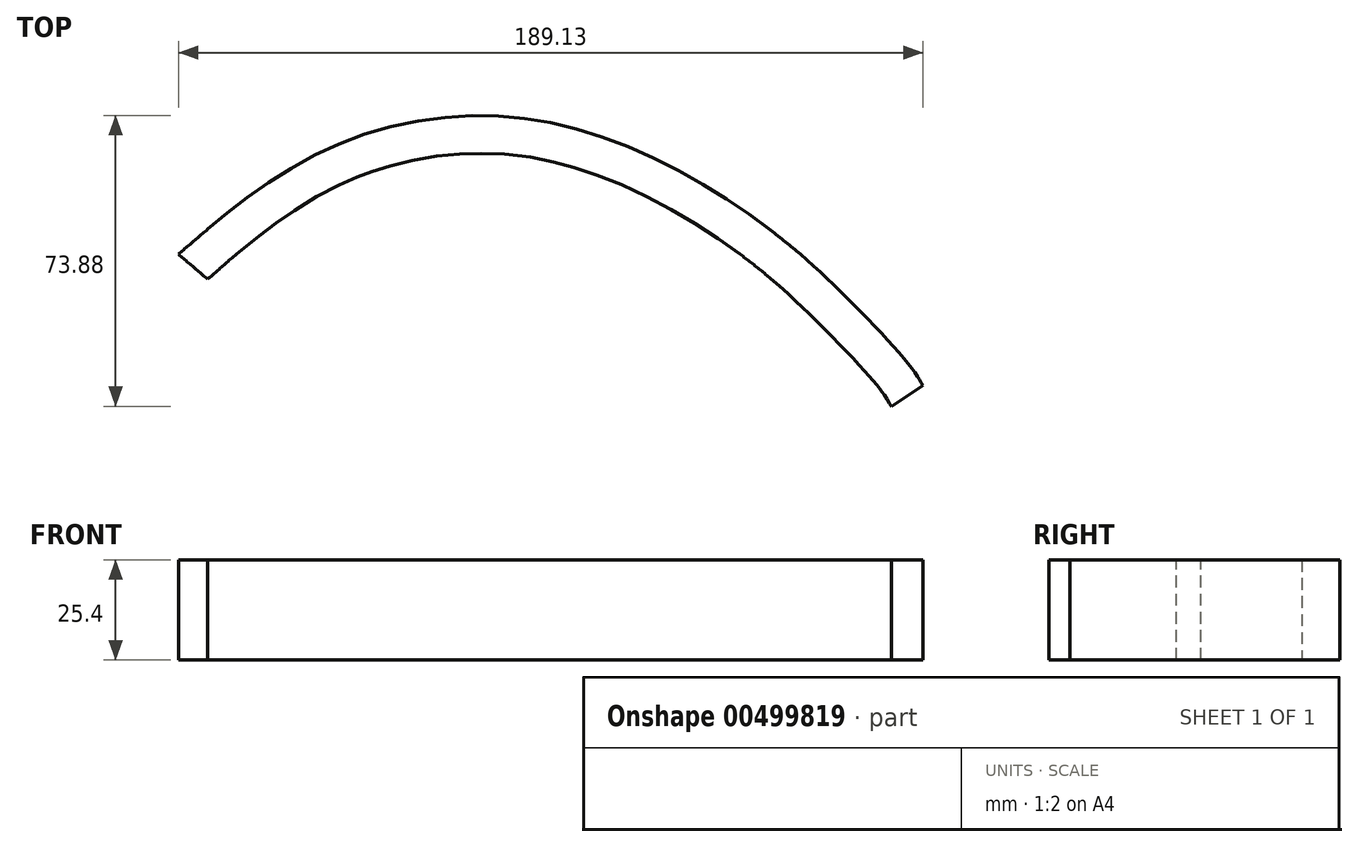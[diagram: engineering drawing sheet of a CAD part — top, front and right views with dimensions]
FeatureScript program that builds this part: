
annotation { "Feature Type Name" : "Feature", "Feature Type Description" : "" }
export const myFeature = defineFeature(function(context is Context, id is Id, definition is map)
    precondition{}
    {
        {
            var Q0;
            Q0=qCreatedBy(makeId("Top.planeOp"),FACE);
            var sketch = newSketch(context, id + "F0", { "sketchPlane" : qUnion([Q0])});
            skFitSpline(sketch, "E0", {"points": [v(0, -39.57) * mm, v(19.12, -23.96) * mm, v(43.28, -10.51) * mm, v(71.59, -4.5) * mm, v(98.2, -6.96) * mm, v(125.64, -17.57) * mm, v(150.11, -33.18) * mm, v(169.77, -50.6) * mm, v(186.21, -68.48) * mm, v(189.13, -72.9) * mm], "startDerivative": vector(163.97, 141.12) * mm, "endDerivative": vector(45.02, -66.87) * mm});
            skLineSegment(sketch, "E1", {"start": v(0, -39.57) * mm, "end": v(190.5, -39.57) * mm, "construction": true});
            skLineSegment(sketch, "E2", {"start": v(181.1, -78.25) * mm, "end": v(189.13, -72.9) * mm});
            skFitSpline(sketch, "E3.0", {"points": [v(3.15, -43.22) * mm, v(6.57, -40.27) * mm, v(11.62, -35.9) * mm, v(17.7, -31.03) * mm, v(21.3, -28.34) * mm, v(24.98, -25.7) * mm, v(29.77, -22.56) * mm, v(35.8, -19.12) * mm, v(41.03, -16.6) * mm, v(45.35, -14.86) * mm, v(49.76, -13.3) * mm, v(55.44, -11.68) * mm, v(62.4, -10.28) * mm, v(68.2, -9.56) * mm, v(72.8, -9.26) * mm, v(77.33, -9.13) * mm, v(82.92, -9.31) * mm, v(89.55, -10.06) * mm, v(95.08, -11.14) * mm, v(99.53, -12.27) * mm, v(104, -13.58) * mm, v(109.61, -15.54) * mm, v(118.55, -19.27) * mm, v(127.3, -23.8) * mm, v(135.62, -28.86) * mm, v(141.59, -32.86) * mm, v(147.23, -37) * mm, v(152.48, -41.19) * mm, v(156.68, -44.83) * mm, v(160.03, -47.9) * mm, v(162.56, -50.3) * mm, v(164.7, -52.37) * mm, v(166.44, -54.1) * mm, v(168.2, -55.85) * mm, v(170.43, -58.1) * mm, v(173.05, -60.82) * mm, v(175.55, -63.48) * mm, v(177.85, -66) * mm, v(179.55, -67.93) * mm, v(180.73, -69.33) * mm, v(181.52, -70.3) * mm, v(182.2, -71.16) * mm, v(182.75, -71.9) * mm, v(183.2, -72.57) * mm, v(183.74, -73.38) * mm, v(184.31, -74.32) * mm, v(184.83, -75.14) * mm, v(185.13, -75.6) * mm], "construction": true});
            skFitSpline(sketch, "E4.MirrorCS", {"points": [v(0, -39.57) * mm, v(19.12, -55.17) * mm, v(43.28, -68.62) * mm, v(71.59, -74.62) * mm, v(98.2, -72.17) * mm, v(125.64, -61.56) * mm, v(150.11, -45.95) * mm, v(169.77, -28.54) * mm, v(186.21, -10.65) * mm, v(189.13, -6.23) * mm], "startDerivative": vector(163.97, -141.12) * mm, "endDerivative": vector(45.02, 66.87) * mm});
            skFitSpline(sketch, "E5.trimOffspring", {"points": [v(6.3, -32.25) * mm, v(9.73, -35.2) * mm, v(14.74, -39.55) * mm, v(20.67, -44.3) * mm, v(24.15, -46.9) * mm, v(27.7, -49.44) * mm, v(32.3, -52.46) * mm, v(38.04, -55.74) * mm, v(42.5, -57.88) * mm, v(45.54, -59.14) * mm, v(47.57, -59.94) * mm, v(50.17, -60.86) * mm, v(53.36, -61.84) * mm, v(57.68, -62.98) * mm, v(63.17, -64.09) * mm, v(68.68, -64.77) * mm, v(73.03, -65.05) * mm, v(77.3, -65.17) * mm, v(82.57, -65) * mm, v(88.82, -64.3) * mm, v(94.03, -63.28) * mm, v(98.25, -62.2) * mm, v(102.5, -60.96) * mm, v(107.88, -59.08) * mm, v(114.33, -56.39) * mm, v(120.7, -53.3) * mm, v(126.96, -49.89) * mm, v(133.02, -46.2) * mm, v(138.82, -42.32) * mm, v(144.3, -38.3) * mm, v(149.39, -34.24) * mm, v(153.47, -30.7) * mm, v(156.74, -27.7) * mm, v(159.22, -25.36) * mm, v(161.32, -23.31) * mm, v(163.04, -21.61) * mm, v(164.78, -19.88) * mm, v(166.98, -17.65) * mm, v(169.56, -14.98) * mm, v(172.01, -12.37) * mm, v(173.89, -10.31) * mm, v(175.25, -8.78) * mm, v(176.18, -7.7) * mm, v(177.03, -6.7) * mm, v(177.76, -5.81) * mm, v(178.26, -5.17) * mm, v(178.6, -4.73) * mm, v(178.89, -4.32) * mm, v(179.2, -3.86) * mm, v(179.65, -3.19) * mm, v(180.07, -2.5) * mm, v(180.61, -1.63) * mm, v(180.94, -1.12) * mm, v(181.12, -0.84) * mm]});
            skFitSpline(sketch, "E6.trimOffspring", {"points": [v(6.3, -46.88) * mm, v(9.73, -43.92) * mm, v(14.74, -39.58) * mm, v(20.67, -34.84) * mm, v(24.15, -32.23) * mm, v(27.7, -29.7) * mm, v(32.3, -26.67) * mm, v(38.04, -23.4) * mm, v(42.5, -21.26) * mm, v(45.54, -20) * mm, v(47.57, -19.2) * mm, v(50.17, -18.27) * mm, v(53.36, -17.3) * mm, v(57.68, -16.15) * mm, v(63.17, -15.04) * mm, v(68.68, -14.37) * mm, v(73.03, -14.08) * mm, v(77.3, -13.96) * mm, v(82.57, -14.13) * mm, v(88.82, -14.84) * mm, v(94.03, -15.85) * mm, v(98.25, -16.93) * mm, v(102.5, -18.17) * mm, v(107.88, -20.05) * mm, v(114.33, -22.74) * mm, v(120.7, -25.82) * mm, v(126.96, -29.24) * mm, v(133.02, -32.93) * mm, v(138.82, -36.81) * mm, v(144.3, -40.83) * mm, v(149.39, -44.9) * mm, v(153.47, -48.44) * mm, v(156.74, -51.43) * mm, v(159.22, -53.77) * mm, v(161.32, -55.82) * mm, v(163.04, -57.52) * mm, v(164.78, -59.25) * mm, v(166.98, -61.48) * mm, v(169.56, -64.15) * mm, v(172.01, -66.76) * mm, v(173.89, -68.82) * mm, v(175.25, -70.35) * mm, v(176.18, -71.43) * mm, v(177.03, -72.42) * mm, v(177.76, -73.32) * mm, v(178.26, -73.96) * mm, v(178.6, -74.4) * mm, v(178.89, -74.8) * mm, v(179.2, -75.27) * mm, v(179.65, -75.95) * mm, v(180.07, -76.63) * mm, v(180.61, -77.5) * mm, v(180.94, -78.01) * mm, v(181.12, -78.29) * mm]});
            skFitSpline(sketch, "E7.trimOffspring", {"points": [v(6.28, -32.27) * mm, v(9.72, -35.22) * mm, v(14.72, -39.56) * mm, v(20.66, -44.31) * mm, v(24.14, -46.92) * mm, v(27.69, -49.46) * mm, v(32.29, -52.48) * mm, v(38.03, -55.76) * mm, v(42.5, -57.9) * mm, v(45.53, -59.16) * mm, v(47.57, -59.96) * mm, v(50.16, -60.88) * mm, v(53.35, -61.86) * mm, v(57.67, -63) * mm, v(63.17, -64.1) * mm, v(68.68, -64.79) * mm, v(73.02, -65.07) * mm, v(77.3, -65.2) * mm, v(82.57, -65.02) * mm, v(88.82, -64.31) * mm, v(94.03, -63.3) * mm, v(98.25, -62.23) * mm, v(102.51, -60.98) * mm, v(107.88, -59.1) * mm, v(114.33, -56.4) * mm, v(120.72, -53.33) * mm, v(126.97, -49.9) * mm, v(133.03, -46.22) * mm, v(138.83, -42.34) * mm, v(144.31, -38.32) * mm, v(149.4, -34.25) * mm, v(153.49, -30.7) * mm, v(156.76, -27.71) * mm, v(159.24, -25.37) * mm, v(161.34, -23.33) * mm, v(163.06, -21.63) * mm, v(164.8, -19.9) * mm, v(167, -17.67) * mm, v(169.57, -15) * mm, v(172.03, -12.38) * mm, v(173.9, -10.33) * mm, v(175.26, -8.8) * mm, v(176.2, -7.72) * mm, v(177.04, -6.72) * mm, v(177.78, -5.83) * mm, v(178.28, -5.18) * mm, v(178.61, -4.74) * mm, v(178.9, -4.34) * mm, v(179.23, -3.88) * mm, v(179.67, -3.2) * mm, v(180.1, -2.5) * mm, v(180.63, -1.64) * mm, v(180.96, -1.13) * mm, v(181.14, -0.86) * mm]});
            skFitSpline(sketch, "E8.trimOffspring", {"points": [v(6.28, -46.86) * mm, v(9.72, -43.9) * mm, v(14.72, -39.57) * mm, v(20.66, -34.82) * mm, v(24.14, -32.21) * mm, v(27.69, -29.67) * mm, v(32.29, -26.66) * mm, v(38.03, -23.37) * mm, v(42.5, -21.24) * mm, v(45.53, -19.97) * mm, v(47.57, -19.17) * mm, v(50.16, -18.25) * mm, v(53.35, -17.27) * mm, v(57.67, -16.13) * mm, v(63.17, -15.02) * mm, v(68.68, -14.34) * mm, v(73.02, -14.06) * mm, v(77.3, -13.94) * mm, v(82.57, -14.1) * mm, v(88.82, -14.82) * mm, v(94.03, -15.83) * mm, v(98.25, -16.9) * mm, v(102.51, -18.15) * mm, v(107.88, -20.03) * mm, v(114.33, -22.72) * mm, v(120.72, -25.8) * mm, v(126.97, -29.22) * mm, v(133.03, -32.9) * mm, v(138.83, -36.8) * mm, v(144.31, -40.8) * mm, v(149.4, -44.88) * mm, v(153.49, -48.42) * mm, v(156.76, -51.42) * mm, v(159.24, -53.76) * mm, v(161.34, -55.8) * mm, v(163.06, -57.5) * mm, v(164.8, -59.24) * mm, v(167, -61.46) * mm, v(169.57, -64.14) * mm, v(172.03, -66.75) * mm, v(173.9, -68.8) * mm, v(175.26, -70.33) * mm, v(176.2, -71.41) * mm, v(177.04, -72.4) * mm, v(177.78, -73.3) * mm, v(178.28, -73.95) * mm, v(178.61, -74.39) * mm, v(178.9, -74.8) * mm, v(179.23, -75.25) * mm, v(179.67, -75.93) * mm, v(180.1, -76.62) * mm, v(180.63, -77.5) * mm, v(180.96, -78) * mm, v(181.14, -78.27) * mm]});
            skFitSpline(sketch, "E9.trimOffspring", {"points": [v(3.15, -35.9) * mm, v(6.57, -38.86) * mm, v(11.62, -43.23) * mm, v(17.7, -48.1) * mm, v(21.3, -50.8) * mm, v(24.98, -53.43) * mm, v(29.77, -56.57) * mm, v(35.8, -60.01) * mm, v(41.03, -62.52) * mm, v(45.35, -64.27) * mm, v(49.76, -65.83) * mm, v(55.44, -67.45) * mm, v(62.4, -68.85) * mm, v(68.2, -69.57) * mm, v(72.8, -69.87) * mm, v(77.33, -70) * mm, v(82.92, -69.82) * mm, v(89.55, -69.07) * mm, v(95.08, -68) * mm, v(99.53, -66.86) * mm, v(104, -65.55) * mm, v(109.61, -63.6) * mm, v(118.55, -59.86) * mm, v(127.3, -55.34) * mm, v(135.62, -50.27) * mm, v(141.59, -46.27) * mm, v(147.23, -42.14) * mm, v(152.48, -37.94) * mm, v(156.68, -34.3) * mm, v(160.03, -31.23) * mm, v(162.56, -28.84) * mm, v(164.7, -26.76) * mm, v(166.44, -25.04) * mm, v(168.2, -23.28) * mm, v(170.43, -21.02) * mm, v(173.05, -18.3) * mm, v(175.55, -15.65) * mm, v(177.85, -13.13) * mm, v(179.55, -11.2) * mm, v(180.73, -9.8) * mm, v(181.52, -8.83) * mm, v(182.2, -7.97) * mm, v(182.75, -7.23) * mm, v(183.2, -6.56) * mm, v(183.74, -5.75) * mm, v(184.31, -4.81) * mm, v(184.83, -3.99) * mm, v(185.13, -3.54) * mm], "construction": true});
            skLineSegment(sketch, "E10", {"start": v(181.1, -0.88) * mm, "end": v(189.13, -6.23) * mm});
            skFitSpline(sketch, "E11.0", {"points": [v(3.15, -35.9) * mm, v(6.58, -38.86) * mm, v(11.62, -43.23) * mm, v(17.7, -48.1) * mm, v(21.3, -50.8) * mm, v(24.98, -53.42) * mm, v(29.77, -56.57) * mm, v(35.8, -60.01) * mm, v(41.03, -62.52) * mm, v(45.35, -64.27) * mm, v(49.76, -65.83) * mm, v(55.44, -67.45) * mm, v(62.4, -68.85) * mm, v(68.2, -69.57) * mm, v(72.8, -69.87) * mm, v(77.33, -70) * mm, v(82.92, -69.82) * mm, v(89.55, -69.07) * mm, v(95.08, -68) * mm, v(99.53, -66.86) * mm, v(104, -65.55) * mm, v(109.61, -63.6) * mm, v(116.31, -60.8) * mm, v(122.92, -57.6) * mm, v(129.37, -54.07) * mm, v(135.62, -50.27) * mm, v(141.59, -46.27) * mm, v(147.23, -42.14) * mm, v(152.48, -37.94) * mm, v(156.68, -34.3) * mm, v(160.03, -31.23) * mm, v(162.56, -28.84) * mm, v(164.7, -26.76) * mm, v(166.44, -25.04) * mm, v(168.2, -23.28) * mm, v(170.43, -21.02) * mm, v(173.05, -18.3) * mm, v(175.55, -15.65) * mm, v(177.85, -13.13) * mm, v(179.55, -11.2) * mm, v(180.73, -9.8) * mm, v(181.52, -8.83) * mm, v(182.2, -7.97) * mm, v(182.75, -7.23) * mm, v(183.2, -6.57) * mm, v(183.6, -5.96) * mm, v(183.9, -5.47) * mm, v(184.15, -5.1) * mm, v(184.39, -4.7) * mm, v(184.7, -4.2) * mm, v(184.98, -3.76) * mm, v(185.13, -3.54) * mm], "construction": true});
            skSolve(sketch);
        }
        {
            var Q0;
            Q0=makeQuery(id+"F0.imprint","IMPRINT",FACE,{"disambiguationData":[TD([[makeQuery(id+"F0.imprint","IMPRINT",EDGE,{"derivedFrom":sQuery(id+"F0.wireOp",EDGE,"E0")}),-1.0]])]});
            extrude(context, id + "F1", {"entities" : qUnion([Q0]), "oppositeDirection" : true, "depth" : 25.4 * mm});
        }
    });
